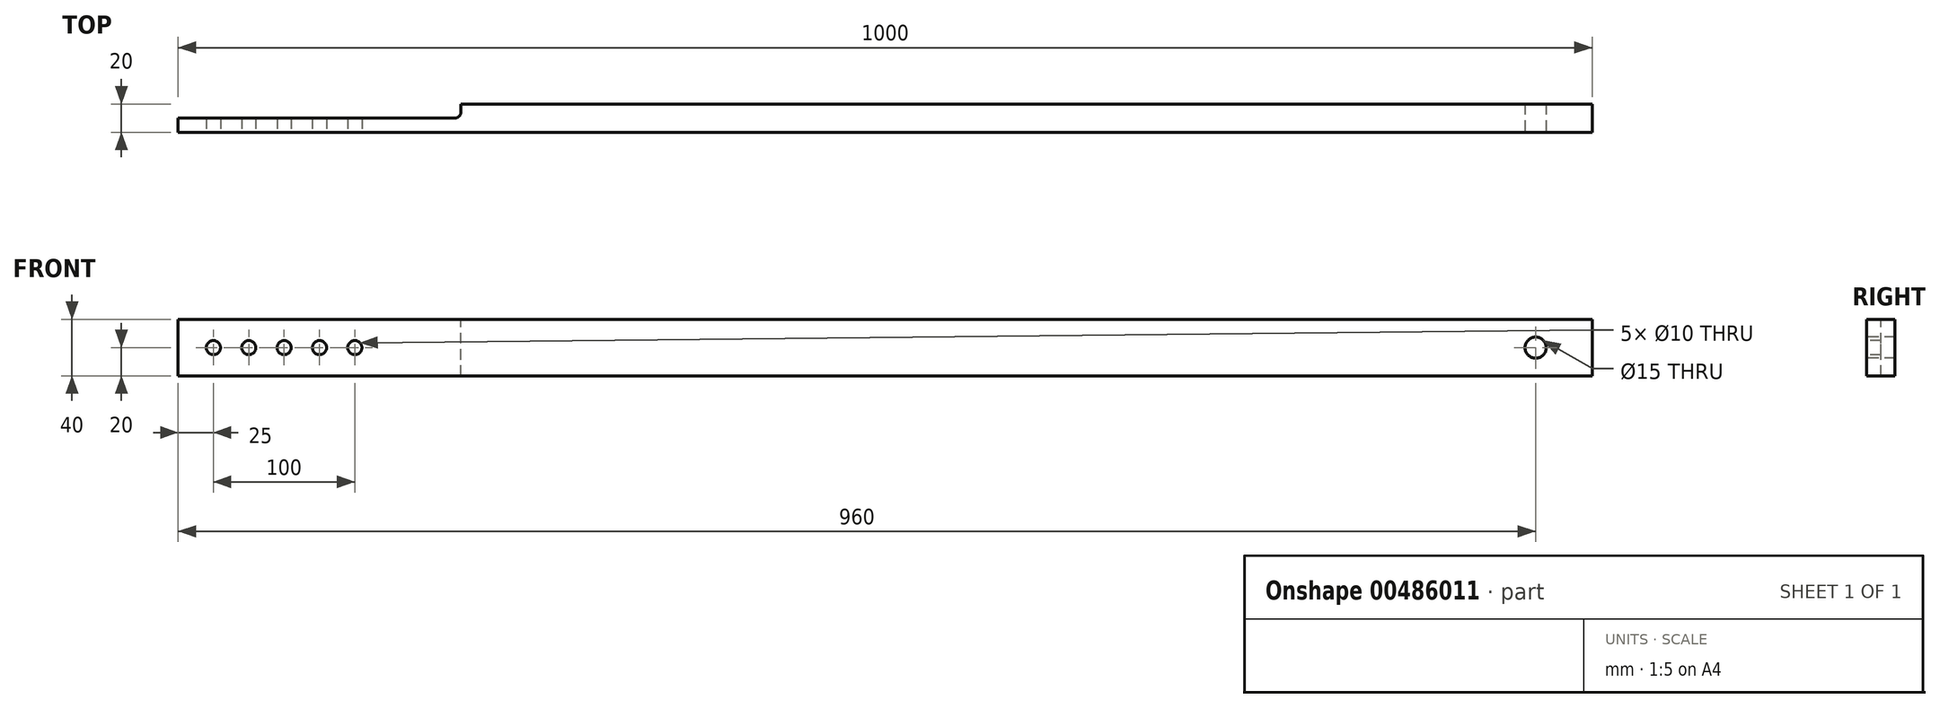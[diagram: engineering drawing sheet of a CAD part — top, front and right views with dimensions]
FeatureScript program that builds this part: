
annotation { "Feature Type Name" : "Feature", "Feature Type Description" : "" }
export const myFeature = defineFeature(function(context is Context, id is Id, definition is map)
    precondition{}
    {
        {
            var Q0;
            Q0=qCreatedBy(makeId("Right.planeOp"),FACE);
            var sketch = newSketch(context, id + "F0", { "sketchPlane" : qUnion([Q0])});
            skLineSegment(sketch, "E0.bottom", {"start": v(10, 20) * mm, "end": v(-10, 20) * mm});
            skLineSegment(sketch, "E0.top", {"start": v(10, -20) * mm, "end": v(-10, -20) * mm});
            skLineSegment(sketch, "E0.left", {"start": v(10, 20) * mm, "end": v(10, -20) * mm});
            skLineSegment(sketch, "E0.right", {"start": v(-10, 20) * mm, "end": v(-10, -20) * mm});
            skPoint(sketch, "E0.middle", {"position": v(0, 0) * mm});
            skSolve(sketch);
        }
        {
            var Q0;
            Q0 = qSketchRegion(id + "F0", true);
            extrude(context, id + "F1", {"entities" : qUnion([Q0]), "endBound" : BoundingType.SYMMETRIC, "depth" : 1000 * mm});
        }
        {
            var Q0;
            Q0=makeQuery(id+"F1.opExtrude","SWEPT_FACE",FACE,{"disambiguationData":[OSD([sQuery(id+"F0.wireOp",EDGE,"E0.right")])]});
            var sketch = newSketch(context, id + "F2", { "sketchPlane" : qUnion([Q0])});
            skCircle(sketch, "E1", {"center": v(460, 0) * mm, "radius": 7.5 * mm});
            skPoint(sketch, "E1.centerSnap0", {"position": v(500, 0) * mm});
            skCircle(sketch, "E2", {"center": v(-475, 0) * mm, "radius": 5 * mm});
            skPoint(sketch, "E2.centerSnap0", {"position": v(-500, 0) * mm});
            skCircle(sketch, "E3", {"center": v(-450, 0) * mm, "radius": 5 * mm});
            skCircle(sketch, "E4", {"center": v(-425, 0) * mm, "radius": 5 * mm});
            skCircle(sketch, "E5", {"center": v(-400, 0) * mm, "radius": 5 * mm});
            skCircle(sketch, "E6", {"center": v(-375, 0) * mm, "radius": 5 * mm});
            skSolve(sketch);
        }
        {
            var Q0;
            Q0 = qSketchRegion(id + "F2", true);
            extrude(context, id + "F3", {"entities" : qUnion([Q0]), "operationType" : NewBodyOperationType.REMOVE, "oppositeDirection" : true, "depth" : 25 * mm});
        }
        {
            var Q0;
            Q0 = qSketchRegion(id + "F2", true);
            extrude(context, id + "F4", {"entities" : qUnion([Q0]), "operationType" : NewBodyOperationType.REMOVE, "oppositeDirection" : true, "depth" : 25 * mm});
        }
        {
            var Q0;
            Q0=makeQuery(id+"F1.opExtrude","SWEPT_FACE",FACE,{"disambiguationData":[OSD([sQuery(id+"F0.wireOp",EDGE,"E0.bottom")])]});
            var sketch = newSketch(context, id + "F5", { "sketchPlane" : qUnion([Q0])});
            skLineSegment(sketch, "E7.bottom", {"start": v(-500, 10) * mm, "end": v(-300, 10) * mm});
            skLineSegment(sketch, "E7.top", {"start": v(-500, 0) * mm, "end": v(-300, 0) * mm});
            skLineSegment(sketch, "E7.left", {"start": v(-500, 10) * mm, "end": v(-500, 0) * mm});
            skLineSegment(sketch, "E7.right", {"start": v(-300, 10) * mm, "end": v(-300, 0) * mm});
            skSolve(sketch);
        }
        {
            var Q0;
            Q0=makeQuery(id+"F5.imprint","IMPRINT",FACE,{"disambiguationData":[TD([[makeQuery(id+"F5.imprint","IMPRINT",EDGE,{"derivedFrom":sQuery(id+"F5.wireOp",EDGE,"E7.bottom")}),1.0]])]});
            extrude(context, id + "F6", {"entities" : qUnion([Q0]), "operationType" : NewBodyOperationType.REMOVE, "endBound" : BoundingType.THROUGH_ALL, "oppositeDirection" : true, "depth" : 25 * mm});
        }
        {
            var Q0;
            Q0=makeQuery(id+"F6.boolean.opBoolean","COPY",EDGE,{"derivedFrom":makeQuery(id+"F6.opExtrude","SWEPT_EDGE",EDGE,{"disambiguationData":[OSD([sQuery(id+"F5.wireOp",EDGE,"E7.top"),sQuery(id+"F5.wireOp",EDGE,"E7.right")])]})});
            fillet(context, id + "F7", {"entities" : qUnion([Q0]), "radius" : 4 * mm, "tangentPropagation" : true, "allowEdgeOverflow" : false});
        }
    });
